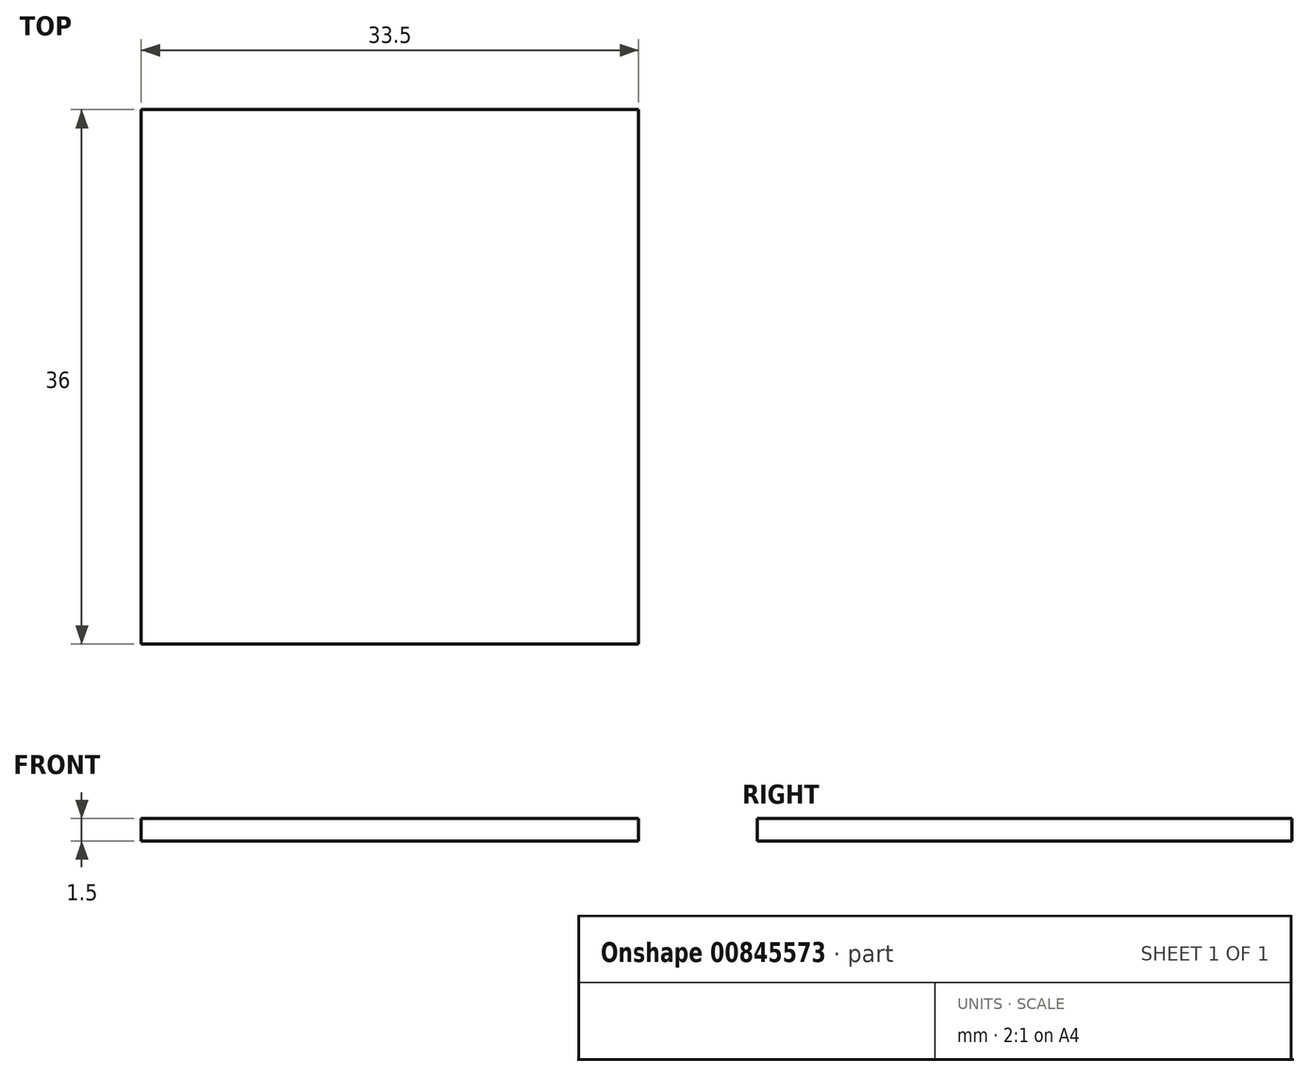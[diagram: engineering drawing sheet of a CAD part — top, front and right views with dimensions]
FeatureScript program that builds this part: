
annotation { "Feature Type Name" : "Feature", "Feature Type Description" : "" }
export const myFeature = defineFeature(function(context is Context, id is Id, definition is map)
    precondition{}
    {
        {
            var Q0;
            Q0=qCreatedBy(makeId("Top.planeOp"),FACE);
            var sketch = newSketch(context, id + "F0", { "sketchPlane" : qUnion([Q0])});
            skLineSegment(sketch, "E0.bottom", {"start": v(-31.37, 47.19) * mm, "end": v(2.13, 47.19) * mm});
            skLineSegment(sketch, "E0.top", {"start": v(-31.37, 11.19) * mm, "end": v(2.13, 11.19) * mm});
            skLineSegment(sketch, "E0.left", {"start": v(-31.37, 47.19) * mm, "end": v(-31.37, 11.19) * mm});
            skLineSegment(sketch, "E0.right", {"start": v(2.13, 47.19) * mm, "end": v(2.13, 11.19) * mm});
            skSolve(sketch);
        }
        {
            var Q0;
            Q0=makeQuery(id+"F0.imprint","IMPRINT",FACE,{"disambiguationData":[TD([[makeQuery(id+"F0.imprint","IMPRINT",EDGE,{"derivedFrom":sQuery(id+"F0.wireOp",EDGE,"E0.bottom")}),-1.0]])]});
            extrude(context, id + "F1", {"entities" : qUnion([Q0]), "depth" : 1.5 * mm, "offsetDistance" : 25 * mm});
        }
    });
